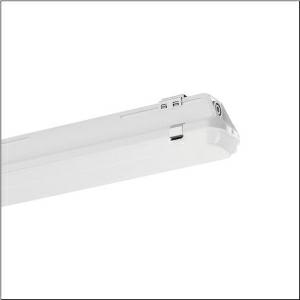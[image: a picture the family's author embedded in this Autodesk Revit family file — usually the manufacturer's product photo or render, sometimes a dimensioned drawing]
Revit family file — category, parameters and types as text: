
# Revit family: monsun_11_51fp10dp4b0u
name_source: partatom
category: Lighting Fixtures
units: mm (PartAtom-declared; Revit-internal decimal feet)

## family parameters
Cut with Voids When Loaded = No
Host = Face
Light Source = No
Part Type = Normal
Room Calculation Point = No
Round Connector Dimension = Use Diameter
Shared = No

## types (1)
- --- (1 x LED, 12110 lm, 63.7 W, 4000K)
    Apparent Load = 64 VA
    CIE Flux Codes = 47 76 93 94 100
    Color Rendering = 80
    Color Temperature = 4000K
    Default Elevation = 1800 mm
    Description = Monsun 11, damp-proof luminaire, chain hanger, primary optical cover: enclosure, of PMMA, light emission: direct distribution, primary light characteristic: symmetric, installation type: suspended mounting, surface-mounted, horizontal mounting, vertical mounting, LED, rated luminous flux: 12.110lm, luminous efficacy: 190lm/W, light colour: 840, colour temperature: 4000K, control gear: DALI 2, with terminal, 5-pole, max. 2.5mm², mains connection: 220..240V, AC, 50/60Hz, rated input power: 64W, luminaire housing, of glass-fibre reinforced polyester, uncoated, bright grey, incl. chain hanger, length: 1.590mm, width: 90mm, height: 88mm, clip for enclosure, of stainless steel (V2A), ceiling mounting element, of stainless steel (V2A), chain hanger, of stainless steel (V2A), protection rating (complete): IP66, insulation class (complete): insulation class I (protective earthing), certification: CE, ENEC, VDE, UKCA, protection symbol: D, impact resistance: IK04, permissible operating ambient temperature: -40..+35°C, standard: EN 50419, EN 60598-2-1, contact your sales advisor before using the luminaires in applications with unclear chemical exposure, large temperature fluctuations or condensation-forming humidity, LABS conformity tested according to VDMA 24364:2018-05, no direct snow, no direct sun, no direct rain, for indoor or canopied outdoor use, corresponds to IFS (International Featured Standards) requirements for safety and quality in the food industry, packaging unit: 1 piece
    Height = 89 mm
    Lamp = 1 x LED
    Lamp Light Flux = 12110 lm
    Lamp Power = 63.7 W
    Lamp count = 1
    Length = 1590 mm
    Luminous efficacy = 190 lm/W
    Manufacturer = Siteco
    ModVariant = No
    Model = 51FP10DP4B0U
    Mounting Place = Ceiling
    Mounting Type = Surface mounted
    Number of Poles = 1
    OnlyDefault = Yes
    Power Factor = 1
    Product Name = Monsun 11
    Product group = damp-proof luminaire
    ProductGroupID = 300
    Protection Class = Protection class I
    Protection Degree = IP 66
    RLX_Detail_Level = 1
    RLX_Emergency_Light_Flux = 0 lm
    RLX_Emergency_Type = 0
    RLX_Emergency_Type_DB = No
    RlxData = <blob elided: 91909 chars, md5=2091760e>
    Socket = socket
    Standby Power = 0 W
    System Light Flux = 12110 lm
    System Power = 64 W
    Type Comments = factory setting: luminous flux: 100 % | dim-lin: 254 | 441 mA
    Type Image = l_1349237.jpg
    URL = http://relux.com
    VarID = @adj_037975
    Voltage = 0 V
    Weight = 0.00 kg
    Width = 90 mm

## geometry (parser evidence)
native form markers: Blend x4, Sweep x14
no freeform markers — native parametric forms only
